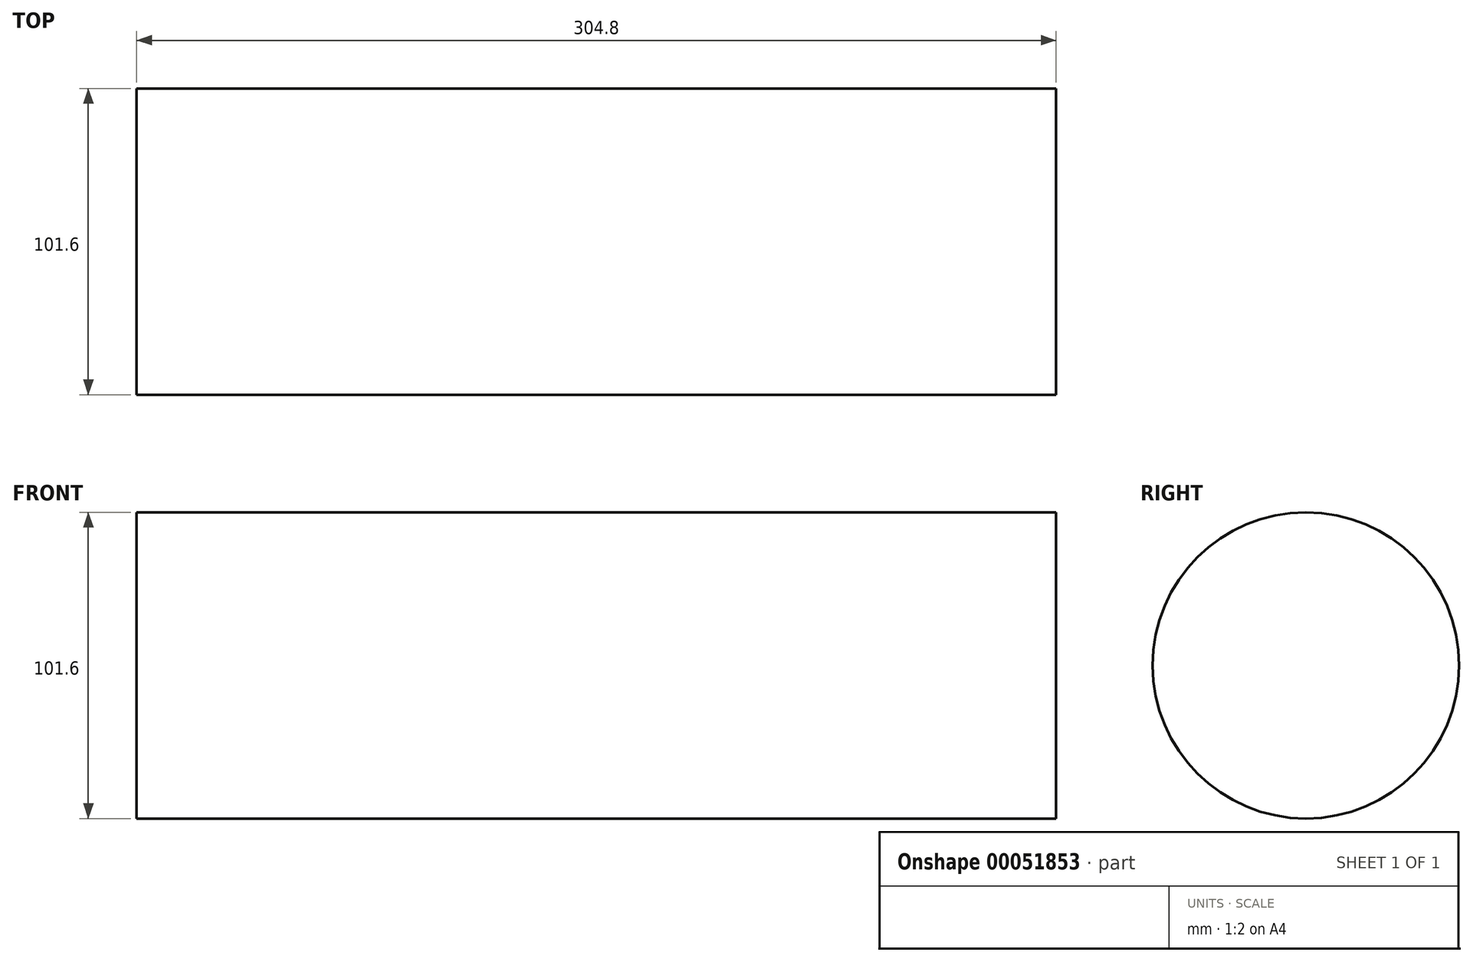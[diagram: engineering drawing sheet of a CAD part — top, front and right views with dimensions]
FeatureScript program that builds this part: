
annotation { "Feature Type Name" : "Feature", "Feature Type Description" : "" }
export const myFeature = defineFeature(function(context is Context, id is Id, definition is map)
    precondition{}
    {
        {
            var Q0;
            Q0=qCreatedBy(makeId("Right.planeOp"),FACE);
            var sketch = newSketch(context, id + "F0", { "sketchPlane" : qUnion([Q0])});
            skCircle(sketch, "E0", {"center": v(0, 0) * mm, "radius": 50.8 * mm});
            skLineSegment(sketch, "E1", {"start": v(48.25, -15.9) * mm, "end": v(-48.25, 15.9) * mm});
            skSolve(sketch);
        }
        {
            var Q0;
            Q0=makeQuery(id+"F0.imprint","IMPRINT",FACE,{"disambiguationData":[TD([[makeQuery(id+"F0.imprint","IMPRINT",EDGE,{"derivedFrom":sQuery(id+"F0.wireOp",EDGE,"E0")}),1.0]])]});
            extrude(context, id + "F1", {"entities" : qUnion([Q0]), "depth" : 304.8 * mm});
        }
        {
            var Q0;
            Q0=makeQuery(id+"F1.opExtrude","SWEPT_BODY",BODY,{"disambiguationData":[OSD([sQuery(id+"F0.wireOp",EDGE,"E0")])]});
            transform(context, id + "F2", {"entities" : qUnion([Q0]), "transformType" : TransformType.TRANSLATION_3D, "dx" : 0 * mm, "dy" : 0 * mm, "dz" : 0 * mm, "makeCopy" : true});
        }
        {
            var Q0;
            Q0=makeQuery(id+"F2.opPattern","COPY",BODY,{"derivedFrom":makeQuery(id+"F1.opExtrude","SWEPT_BODY",BODY,{"disambiguationData":[OSD([sQuery(id+"F0.wireOp",EDGE,"E0")])]}),"instanceName":"1"});
            deleteBodies(context, id + "F3", {"entities" : qUnion([Q0])});
        }
    });
